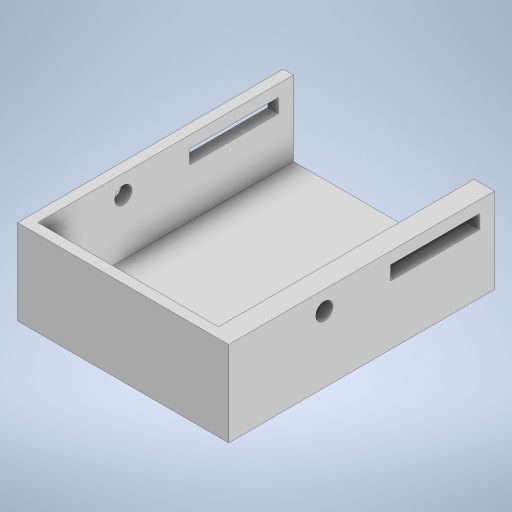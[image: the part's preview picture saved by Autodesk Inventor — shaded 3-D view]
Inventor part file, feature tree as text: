
AUTODESK INVENTOR PART (.ipt)
format: ipt  version: 2023 (Build 270158000, 158)  size: 252,416 bytes
history: native  units: in
note: dims shown in document units (in); Inventor stores cm internally (conversion verified against a paired STEP export)
features: sketch x6, extrude x5, shell x1
ambient origin geometry x8: Origin, YZ Plane, XZ Plane, XY Plane, X Axis, Y Axis, Z Axis, Center Point
bodies: Solid1 (feature_tree)
feature tree (12):
  extrude  "Extrusion1"  Depth=3.0709in
  shell  "Shell1"  Thickness=0.9843in
  sketch  "Sketch4"  dims[d4=0.1181in d17=0.3937in d18=0.0in]
  extrude  "Extrusion3"  Depth=0.3937in TaperAngle=0.0deg
  sketch  "Sketch6"  dims[d21=0.1772in d22=0.689in]
  extrude  "Extrusion5"  Depth=0.1575in
  extrude  "Extrusion6"  Depth=0.689in
  extrude  "Extrusion7"  TaperAngle=0.0deg  [1 undecoded]
  sketch  "Sketch2"  dims[d0=2.3228in d1=3.0709in d2=0.9843in d3=0.0in]
  sketch  "Sketch5"  dims[d19=1.0236in d20=0.1575in]
  sketch  "Sketch7"  dims[d25=0.1181in d26=0.0in d27=0.0in d28=0.0in]
  sketch  "Sketch8"  dims[d29=0.1969in d30=0.0in d31=0.0in d13=0.0197in d14=0.0344in d15=0.0197in d16=0.0344in d32=0.0197in d33=0.0344in]
note: 1 required parameter value undecoded (feature->parameter linkage not recoverable at this tier; creation-order binding heuristic only, values carry confidence <= 0.55)
